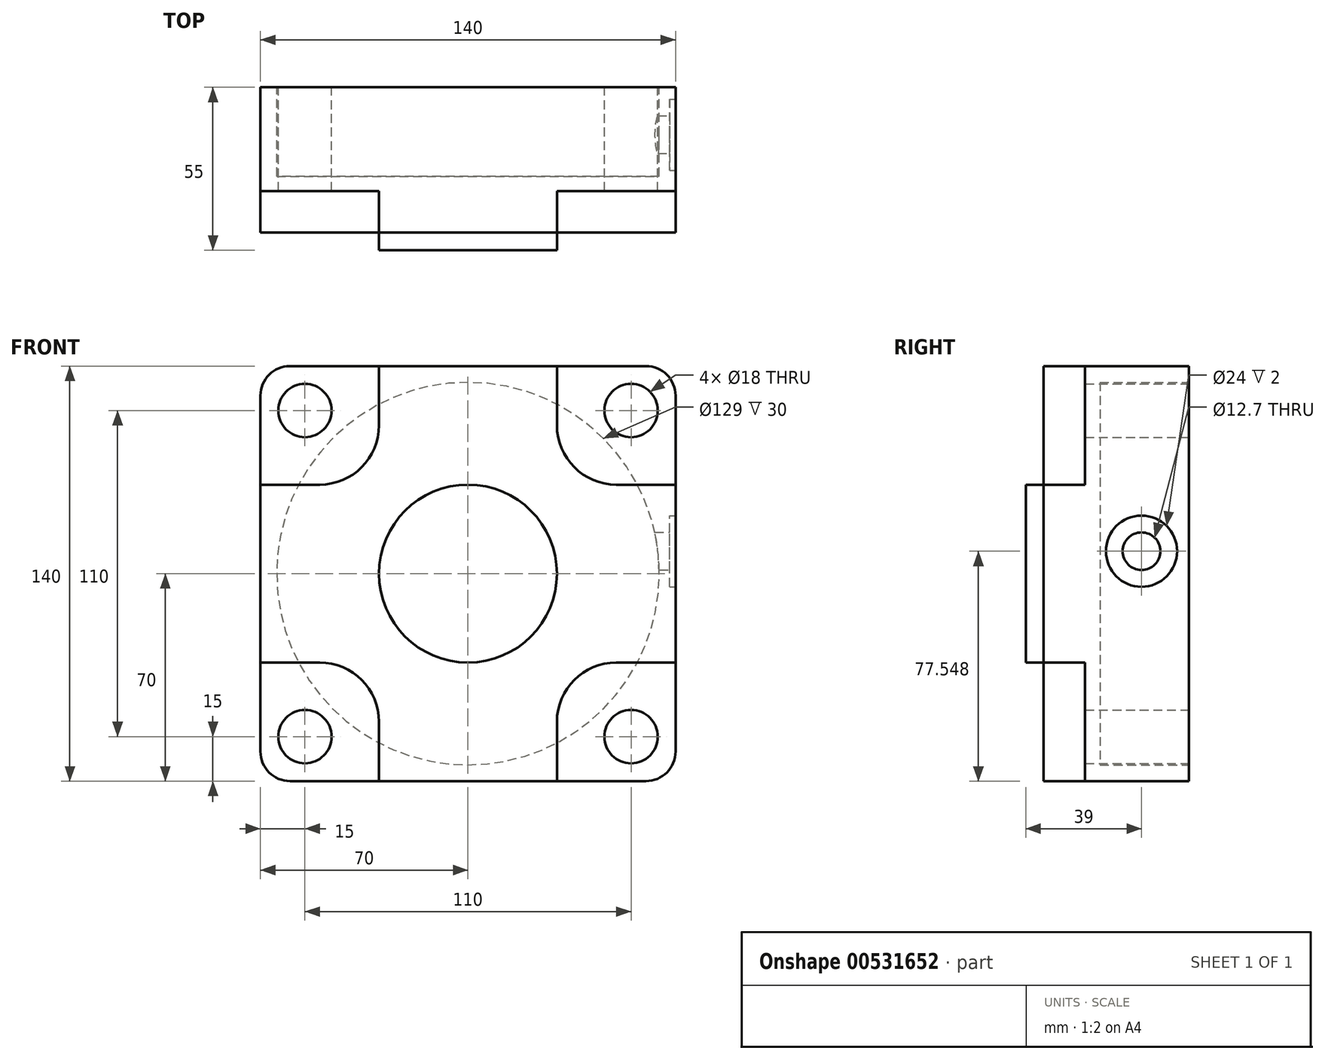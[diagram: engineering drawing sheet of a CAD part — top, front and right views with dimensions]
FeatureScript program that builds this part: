
annotation { "Feature Type Name" : "Feature", "Feature Type Description" : "" }
export const myFeature = defineFeature(function(context is Context, id is Id, definition is map)
    precondition{}
    {
        {
            var Q0;
            Q0=qCreatedBy(makeId("Front.planeOp"),FACE);
            var sketch = newSketch(context, id + "F0", { "sketchPlane" : qUnion([Q0])});
            skLineSegment(sketch, "E0.bottom", {"start": v(60, -70) * mm, "end": v(-60, -70) * mm});
            skLineSegment(sketch, "E0.top", {"start": v(60, 70) * mm, "end": v(-60, 70) * mm});
            skLineSegment(sketch, "E0.left", {"start": v(70, -60) * mm, "end": v(70, 60) * mm});
            skLineSegment(sketch, "E0.right", {"start": v(-70, -60) * mm, "end": v(-70, 60) * mm});
            skPoint(sketch, "E0.middle", {"position": v(0, 0) * mm});
            skPoint(sketch, "E1.visualSharp", {"position": v(-70, 70) * mm});
            skArc(sketch, "E1.filletArc", {"start": v(-60, 70) * mm, "mid": v(-67.07, 67.07) * mm, "end": v(-70, 60) * mm});
            skPoint(sketch, "E2.visualSharp", {"position": v(70, 70) * mm});
            skArc(sketch, "E2.filletArc", {"start": v(70, 60) * mm, "mid": v(67.07, 67.07) * mm, "end": v(60, 70) * mm});
            skPoint(sketch, "E3.visualSharp", {"position": v(70, -70) * mm});
            skArc(sketch, "E3.filletArc", {"start": v(60, -70) * mm, "mid": v(67.07, -67.07) * mm, "end": v(70, -60) * mm});
            skPoint(sketch, "E4.visualSharp", {"position": v(-70, -70) * mm});
            skArc(sketch, "E4.filletArc", {"start": v(-70, -60) * mm, "mid": v(-67.07, -67.07) * mm, "end": v(-60, -70) * mm});
            skLineSegment(sketch, "E5", {"start": v(0, 70) * mm, "end": v(0, -70) * mm, "construction": true});
            skLineSegment(sketch, "E6.0", {"start": v(-55, 47.5) * mm, "end": v(-55, -47.5) * mm, "construction": true});
            skLineSegment(sketch, "E7.0", {"start": v(55, 47.5) * mm, "end": v(55, -47.5) * mm, "construction": true});
            skLineSegment(sketch, "E8", {"start": v(-70, 0) * mm, "end": v(70, 0) * mm, "construction": true});
            skLineSegment(sketch, "E9.0", {"start": v(-47.5, -55) * mm, "end": v(47.5, -55) * mm, "construction": true});
            skLineSegment(sketch, "E10.0", {"start": v(-47.5, 55) * mm, "end": v(47.5, 55) * mm, "construction": true});
            skCircle(sketch, "E11", {"center": v(-55, 55) * mm, "radius": 9 * mm});
            skCircle(sketch, "E12", {"center": v(55, 55) * mm, "radius": 9 * mm});
            skCircle(sketch, "E13", {"center": v(-55, -55) * mm, "radius": 9 * mm});
            skCircle(sketch, "E14", {"center": v(55, -55) * mm, "radius": 9 * mm});
            skSolve(sketch);
        }
        {
            var Q0;
            Q0=makeQuery(id+"F0.imprint","IMPRINT",FACE,{"disambiguationData":[TD([[makeQuery(id+"F0.imprint","IMPRINT",EDGE,{"derivedFrom":sQuery(id+"F0.wireOp",EDGE,"E0.bottom")}),-1.0]])]});
            extrude(context, id + "F1", {"entities" : qUnion([Q0]), "endBound" : BoundingType.SYMMETRIC, "depth" : 49 * mm, "offsetDistance" : 25 * mm});
        }
        {
            var Q0;
            Q0=makeQuery(id+"F1.opExtrude","CAP_FACE",FACE,{"disambiguationData":[OSD([sQuery(id+"F0.wireOp",EDGE,"E0.bottom"),sQuery(id+"F0.wireOp",EDGE,"E0.top"),sQuery(id+"F0.wireOp",EDGE,"E0.left"),sQuery(id+"F0.wireOp",EDGE,"E0.right"),sQuery(id+"F0.wireOp",EDGE,"E1.filletArc"),sQuery(id+"F0.wireOp",EDGE,"E2.filletArc"),sQuery(id+"F0.wireOp",EDGE,"E3.filletArc"),sQuery(id+"F0.wireOp",EDGE,"E4.filletArc"),sQuery(id+"F0.wireOp",EDGE,"E11"),sQuery(id+"F0.wireOp",EDGE,"E12"),sQuery(id+"F0.wireOp",EDGE,"E13"),sQuery(id+"F0.wireOp",EDGE,"E14")])],"isStart":false});
            var sketch = newSketch(context, id + "F2", { "sketchPlane" : qUnion([Q0])});
            skLineSegment(sketch, "E15", {"start": v(-70, 30) * mm, "end": v(-50, 30) * mm});
            skLineSegment(sketch, "E16", {"start": v(-70, -30) * mm, "end": v(-50, -30) * mm});
            skLineSegment(sketch, "E17", {"start": v(-30, 70) * mm, "end": v(-30, 50) * mm});
            skLineSegment(sketch, "E18", {"start": v(30, 70) * mm, "end": v(30, 50) * mm});
            skLineSegment(sketch, "E19", {"start": v(50, 30) * mm, "end": v(70, 30) * mm});
            skLineSegment(sketch, "E20", {"start": v(50, -30) * mm, "end": v(70, -30) * mm});
            skLineSegment(sketch, "E21", {"start": v(30, -50) * mm, "end": v(30, -70) * mm});
            skLineSegment(sketch, "E22", {"start": v(-30, -50) * mm, "end": v(-30, -70) * mm});
            skArc(sketch, "E23.filletArc", {"start": v(-50, 30) * mm, "mid": v(-35.86, 35.86) * mm, "end": v(-30, 50) * mm});
            skPoint(sketch, "E24.newPointA", {"position": v(0.48, 30) * mm});
            skArc(sketch, "E24.filletArc", {"start": v(30, 50) * mm, "mid": v(35.86, 35.86) * mm, "end": v(50, 30) * mm});
            skPoint(sketch, "E25.newPointB", {"position": v(-30, -0.08) * mm});
            skArc(sketch, "E25.filletArc", {"start": v(-30, -50) * mm, "mid": v(-35.86, -35.86) * mm, "end": v(-50, -30) * mm});
            skPoint(sketch, "E26.newPointA", {"position": v(1.13, -30) * mm});
            skPoint(sketch, "E26.newPointB", {"position": v(30, -0.08) * mm});
            skArc(sketch, "E26.filletArc", {"start": v(50, -30) * mm, "mid": v(35.86, -35.86) * mm, "end": v(30, -50) * mm});
            skLineSegment(sketch, "E27.0", {"start": v(-70, -60) * mm, "end": v(-70, -30) * mm});
            skArc(sketch, "E28.0", {"start": v(-60, 70) * mm, "mid": v(-67.07, 67.07) * mm, "end": v(-70, 60) * mm});
            skLineSegment(sketch, "E29.0", {"start": v(60, 70) * mm, "end": v(30, 70) * mm});
            skPoint(sketch, "E30.0", {"position": v(67.07, 67.07) * mm});
            skArc(sketch, "E31.0", {"start": v(70, 60) * mm, "mid": v(67.07, 67.07) * mm, "end": v(60, 70) * mm});
            skLineSegment(sketch, "E32.0", {"start": v(70, -60) * mm, "end": v(70, -30) * mm});
            skPoint(sketch, "E33.0", {"position": v(67.07, -67.07) * mm});
            skArc(sketch, "E34.0", {"start": v(60, -70) * mm, "mid": v(67.07, -67.07) * mm, "end": v(70, -60) * mm});
            skLineSegment(sketch, "E35.0", {"start": v(60, -70) * mm, "end": v(30, -70) * mm});
            skArc(sketch, "E36.0", {"start": v(-70, -60) * mm, "mid": v(-67.07, -67.07) * mm, "end": v(-60, -70) * mm});
            skPoint(sketch, "E37.orphan", {"position": v(-51.1, 30) * mm});
            skPoint(sketch, "E38.orphan", {"position": v(-30, 52.95) * mm});
            skLineSegment(sketch, "E39.trimOffspring", {"start": v(-30, 70) * mm, "end": v(-60, 70) * mm});
            skLineSegment(sketch, "E40.trimOffspring", {"start": v(-70, 30) * mm, "end": v(-70, 60) * mm});
            skPoint(sketch, "E41.orphan", {"position": v(-30, -53.12) * mm});
            skPoint(sketch, "E42.orphan", {"position": v(-51.1, -30) * mm});
            skLineSegment(sketch, "E43.trimOffspring", {"start": v(-30, -70) * mm, "end": v(-60, -70) * mm});
            skPoint(sketch, "E44.orphan", {"position": v(30, -51.66) * mm});
            skPoint(sketch, "E45.orphan", {"position": v(53.36, -30) * mm});
            skPoint(sketch, "E46.orphan", {"position": v(52.07, 30) * mm});
            skPoint(sketch, "E47.orphan", {"position": v(30, 51.5) * mm});
            skLineSegment(sketch, "E48.trimOffspring", {"start": v(70, 30) * mm, "end": v(70, 60) * mm});
            skSolve(sketch);
        }
        {
            var Q0;
            Q0=makeQuery(id+"F2.imprint","IMPRINT",FACE,{"disambiguationData":[TD([[makeQuery(id+"F2.imprint","IMPRINT",EDGE,{"derivedFrom":sQuery(id+"F2.wireOp",EDGE,"E20")}),-1.0]])]});
            var Q1;
            Q1=makeQuery(id+"F2.imprint","IMPRINT",FACE,{"disambiguationData":[TD([[makeQuery(id+"F2.imprint","IMPRINT",EDGE,{"derivedFrom":sQuery(id+"F2.wireOp",EDGE,"E18")}),1.0]])]});
            var Q2;
            Q2=makeQuery(id+"F2.imprint","IMPRINT",FACE,{"disambiguationData":[TD([[makeQuery(id+"F2.imprint","IMPRINT",EDGE,{"derivedFrom":sQuery(id+"F2.wireOp",EDGE,"E15")}),1.0]])]});
            var Q3;
            Q3=makeQuery(id+"F2.imprint","IMPRINT",FACE,{"disambiguationData":[TD([[makeQuery(id+"F2.imprint","IMPRINT",EDGE,{"derivedFrom":sQuery(id+"F2.wireOp",EDGE,"E16")}),-1.0]])]});
            extrude(context, id + "F3", {"entities" : qUnion([Q0, Q1, Q2, Q3]), "operationType" : NewBodyOperationType.REMOVE, "oppositeDirection" : true, "depth" : 14 * mm, "offsetDistance" : 25 * mm});
        }
        {
            var Q0;
            Q0=makeQuery(id+"F1.opExtrude","CAP_FACE",FACE,{"disambiguationData":[OSD([sQuery(id+"F0.wireOp",EDGE,"E0.bottom"),sQuery(id+"F0.wireOp",EDGE,"E0.top"),sQuery(id+"F0.wireOp",EDGE,"E0.left"),sQuery(id+"F0.wireOp",EDGE,"E0.right"),sQuery(id+"F0.wireOp",EDGE,"E1.filletArc"),sQuery(id+"F0.wireOp",EDGE,"E2.filletArc"),sQuery(id+"F0.wireOp",EDGE,"E3.filletArc"),sQuery(id+"F0.wireOp",EDGE,"E4.filletArc"),sQuery(id+"F0.wireOp",EDGE,"E11"),sQuery(id+"F0.wireOp",EDGE,"E12"),sQuery(id+"F0.wireOp",EDGE,"E13"),sQuery(id+"F0.wireOp",EDGE,"E14")])],"isStart":false});
            var sketch = newSketch(context, id + "F4", { "sketchPlane" : qUnion([Q0])});
            skCircle(sketch, "E49", {"center": v(0, 0) * mm, "radius": 30 * mm});
            skSolve(sketch);
        }
        {
            var Q0;
            Q0=makeQuery(id+"F4.imprint","IMPRINT",FACE,{"disambiguationData":[TD([[makeQuery(id+"F4.imprint","IMPRINT",EDGE,{"derivedFrom":sQuery(id+"F4.wireOp",EDGE,"E49")}),1.0]])]});
            extrude(context, id + "F5", {"entities" : qUnion([Q0]), "operationType" : NewBodyOperationType.ADD, "depth" : 6 * mm, "offsetDistance" : 25 * mm});
        }
        {
            var Q0;
            Q0=makeQuery(id+"F1.opExtrude","CAP_FACE",FACE,{"disambiguationData":[OSD([sQuery(id+"F0.wireOp",EDGE,"E0.bottom"),sQuery(id+"F0.wireOp",EDGE,"E0.top"),sQuery(id+"F0.wireOp",EDGE,"E0.left"),sQuery(id+"F0.wireOp",EDGE,"E0.right"),sQuery(id+"F0.wireOp",EDGE,"E1.filletArc"),sQuery(id+"F0.wireOp",EDGE,"E2.filletArc"),sQuery(id+"F0.wireOp",EDGE,"E3.filletArc"),sQuery(id+"F0.wireOp",EDGE,"E4.filletArc"),sQuery(id+"F0.wireOp",EDGE,"E11"),sQuery(id+"F0.wireOp",EDGE,"E12"),sQuery(id+"F0.wireOp",EDGE,"E13"),sQuery(id+"F0.wireOp",EDGE,"E14")])],"isStart":true});
            var sketch = newSketch(context, id + "F6", { "sketchPlane" : qUnion([Q0])});
            skCircle(sketch, "E50", {"center": v(0, 0) * mm, "radius": 64.5 * mm});
            skSolve(sketch);
        }
        {
            var Q0;
            Q0=makeQuery(id+"F1.opExtrude","SWEPT_FACE",FACE,{"disambiguationData":[OSD([sQuery(id+"F0.wireOp",EDGE,"E0.left")])]});
            var sketch = newSketch(context, id + "F7", { "sketchPlane" : qUnion([Q0])});
            skLineSegment(sketch, "E51", {"start": v(8.5, 48.9) * mm, "end": v(8.5, -49.62) * mm, "construction": true});
            skCircle(sketch, "E52", {"center": v(8.5, 7.55) * mm, "radius": 6.35 * mm});
            skCircle(sketch, "E53", {"center": v(8.5, 7.55) * mm, "radius": 12 * mm});
            skSolve(sketch);
        }
        {
            var Q0;
            Q0=makeQuery(id+"F6.imprint","IMPRINT",FACE,{"disambiguationData":[TD([[makeQuery(id+"F6.imprint","IMPRINT",EDGE,{"derivedFrom":sQuery(id+"F6.wireOp",EDGE,"E50")}),1.0]])]});
            extrude(context, id + "F8", {"entities" : qUnion([Q0]), "operationType" : NewBodyOperationType.REMOVE, "oppositeDirection" : true, "depth" : 30 * mm, "offsetDistance" : 25 * mm});
        }
        {
            var Q0;
            Q0=makeQuery(id+"F7.imprint","IMPRINT",FACE,{"disambiguationData":[TD([[makeQuery(id+"F7.imprint","IMPRINT",EDGE,{"derivedFrom":sQuery(id+"F7.wireOp",EDGE,"E52")}),-1.0]])]});
            extrude(context, id + "F9", {"entities" : qUnion([Q0]), "operationType" : NewBodyOperationType.REMOVE, "oppositeDirection" : true, "depth" : 2 * mm});
        }
        {
            var Q0;
            Q0=makeQuery(id+"F9.boolean.opBoolean","SPLIT",FACE,{"disambiguationData":[TD([makeQuery(id+"F9.opExtrude","SWEPT_FACE",FACE,{"disambiguationData":[OSD([sQuery(id+"F7.wireOp",EDGE,"E52")])]})])],"derivedFrom":makeQuery(id+"F1.opExtrude","SWEPT_FACE",FACE,{"disambiguationData":[OSD([sQuery(id+"F0.wireOp",EDGE,"E0.left")])]})});
            extrude(context, id + "F10", {"entities" : qUnion([Q0]), "operationType" : NewBodyOperationType.REMOVE, "oppositeDirection" : true, "depth" : 8 * mm});
        }
    });
